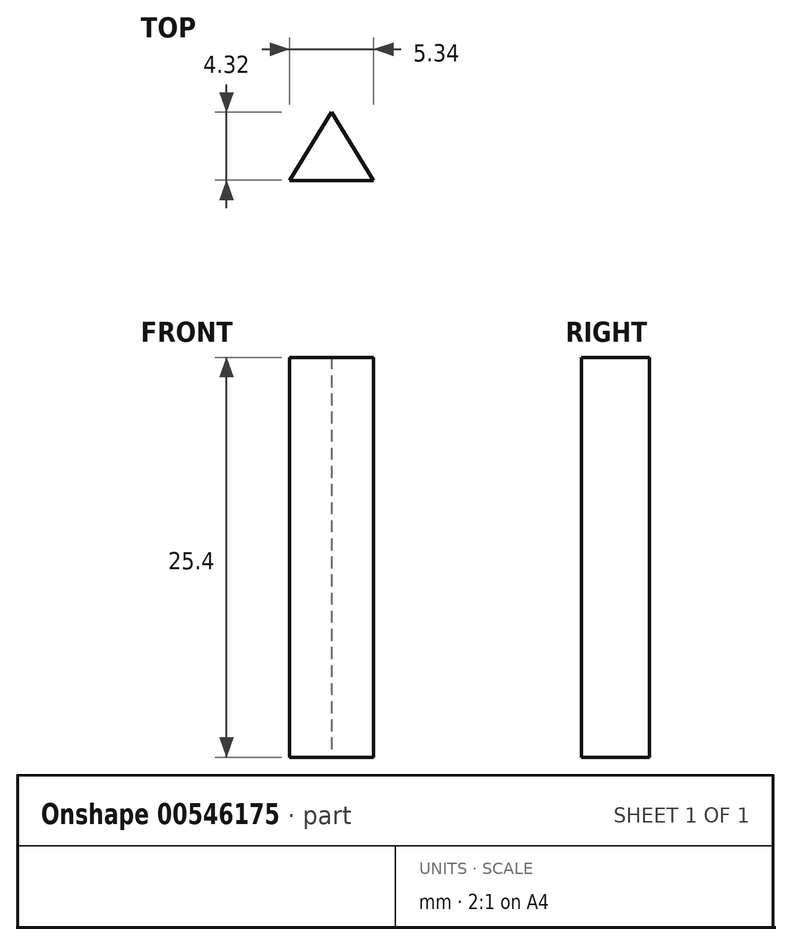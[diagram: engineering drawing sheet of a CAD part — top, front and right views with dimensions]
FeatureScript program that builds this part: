
annotation { "Feature Type Name" : "Feature", "Feature Type Description" : "" }
export const myFeature = defineFeature(function(context is Context, id is Id, definition is map)
    precondition{}
    {
        {
            var Q0;
            Q0=qCreatedBy(makeId("Top.planeOp"),FACE);
            var sketch = newSketch(context, id + "F0", { "sketchPlane" : qUnion([Q0])});
            skLineSegment(sketch, "E0", {"start": v(0, 0) * mm, "end": v(2.67, -4.32) * mm});
            skLineSegment(sketch, "E1", {"start": v(2.67, -4.32) * mm, "end": v(-2.67, -4.32) * mm});
            skLineSegment(sketch, "E2", {"start": v(0, 0) * mm, "end": v(-2.67, -4.32) * mm});
            skSolve(sketch);
        }
        {
            var Q0;
            Q0=makeQuery(id+"F0.imprint","IMPRINT",FACE,{"disambiguationData":[TD([[makeQuery(id+"F0.imprint","IMPRINT",EDGE,{"derivedFrom":sQuery(id+"F0.wireOp",EDGE,"E0")}),-1.0]])]});
            extrude(context, id + "F1", {"entities" : qUnion([Q0]), "depth" : 25.4 * mm, "offsetDistance" : 25.4 * mm});
        }
    });
